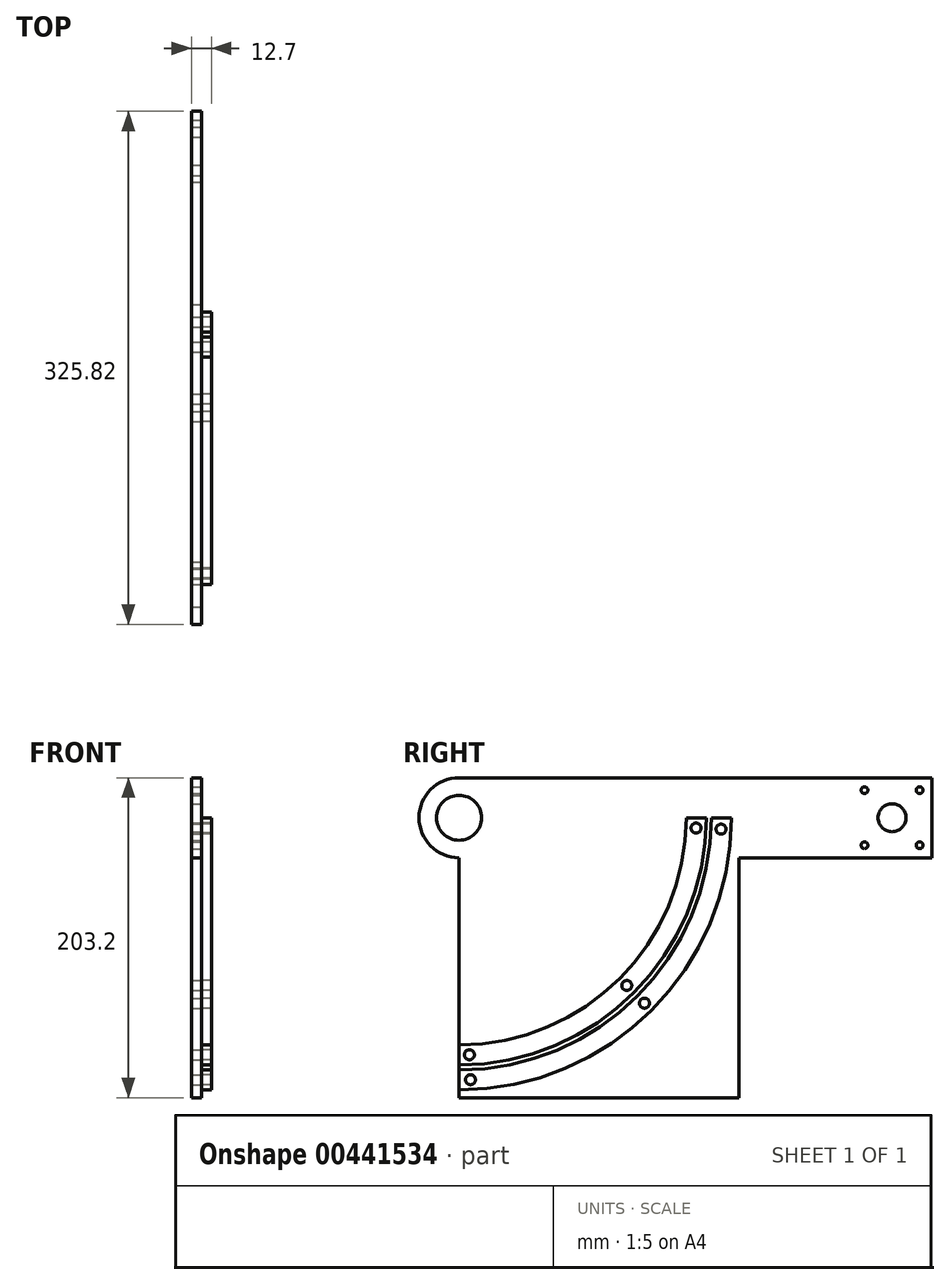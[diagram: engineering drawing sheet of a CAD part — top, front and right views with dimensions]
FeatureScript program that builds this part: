
annotation { "Feature Type Name" : "Feature", "Feature Type Description" : "" }
export const myFeature = defineFeature(function(context is Context, id is Id, definition is map)
    precondition{}
    {
        {
            var Q0;
            Q0=qCreatedBy(makeId("Right.planeOp"),FACE);
            var sketch = newSketch(context, id + "F0", { "sketchPlane" : qUnion([Q0])});
            skCircle(sketch, "E0", {"center": v(-106.55, 177.8) * mm, "radius": 25.4 * mm});
            skCircle(sketch, "E1", {"center": v(-106.55, 177.8) * mm, "radius": 14.29 * mm});
            skLineSegment(sketch, "E2.bottom", {"start": v(-106.55, 177.8) * mm, "end": v(71.25, 177.8) * mm});
            skLineSegment(sketch, "E2.top", {"start": v(-106.55, 0) * mm, "end": v(71.25, 0) * mm});
            skLineSegment(sketch, "E2.left", {"start": v(-106.55, 177.8) * mm, "end": v(-106.55, 0) * mm});
            skLineSegment(sketch, "E2.right", {"start": v(71.25, 177.8) * mm, "end": v(71.25, 0) * mm});
            skCircle(sketch, "E3", {"center": v(168.47, 177.8) * mm, "radius": 8.9 * mm});
            skLineSegment(sketch, "E4.bottom", {"start": v(185.97, 195.3) * mm, "end": v(150.97, 195.3) * mm, "construction": true});
            skLineSegment(sketch, "E4.top", {"start": v(185.97, 160.3) * mm, "end": v(150.97, 160.3) * mm, "construction": true});
            skLineSegment(sketch, "E4.left", {"start": v(185.97, 195.3) * mm, "end": v(185.97, 160.3) * mm, "construction": true});
            skLineSegment(sketch, "E4.right", {"start": v(150.97, 195.3) * mm, "end": v(150.97, 160.3) * mm, "construction": true});
            skCircle(sketch, "E5", {"center": v(185.97, 195.3) * mm, "radius": 2.16 * mm});
            skCircle(sketch, "E6", {"center": v(185.97, 160.3) * mm, "radius": 2.16 * mm});
            skCircle(sketch, "E7", {"center": v(150.97, 160.3) * mm, "radius": 2.16 * mm});
            skCircle(sketch, "E8", {"center": v(150.97, 195.3) * mm, "radius": 2.16 * mm});
            skArc(sketch, "E9", {"start": v(-106.55, 20.76) * mm, "mid": v(4.5, 66.76) * mm, "end": v(50.48, 177.8) * mm});
            skArc(sketch, "E10.0", {"start": v(-106.55, 11.24) * mm, "mid": v(11.23, 60.02) * mm, "end": v(60, 177.8) * mm, "construction": true});
            skArc(sketch, "E11.0", {"start": v(-106.55, 27.11) * mm, "mid": v(0, 71.25) * mm, "end": v(44.13, 177.8) * mm, "construction": true});
            skCircle(sketch, "E12", {"center": v(-99.98, 27.26) * mm, "radius": 3.18 * mm});
            skCircle(sketch, "E13", {"center": v(-99.29, 11.4) * mm, "radius": 3.18 * mm});
            skCircle(sketch, "E14", {"center": v(0, 71.25) * mm, "radius": 3.18 * mm});
            skCircle(sketch, "E15", {"center": v(11.23, 60.02) * mm, "radius": 3.18 * mm});
            skCircle(sketch, "E16", {"center": v(44, 171.23) * mm, "radius": 3.18 * mm});
            skCircle(sketch, "E17", {"center": v(59.85, 170.53) * mm, "radius": 3.18 * mm});
            skLineSegment(sketch, "E18", {"start": v(-106.55, 177.8) * mm, "end": v(59.85, 170.53) * mm, "construction": true});
            skLineSegment(sketch, "E19", {"start": v(11.23, 60.02) * mm, "end": v(-106.55, 177.8) * mm, "construction": true});
            skLineSegment(sketch, "E20", {"start": v(-99.29, 11.4) * mm, "end": v(-106.55, 177.8) * mm, "construction": true});
            skArc(sketch, "E21.0", {"start": v(-106.55, 33.46) * mm, "mid": v(-4.5, 75.74) * mm, "end": v(37.78, 177.8) * mm});
            skArc(sketch, "E22.0", {"start": v(-106.55, 17.59) * mm, "mid": v(6.74, 64.51) * mm, "end": v(53.66, 177.8) * mm});
            skArc(sketch, "E23.0", {"start": v(-106.55, 4.89) * mm, "mid": v(15.72, 55.53) * mm, "end": v(66.36, 177.8) * mm});
            skLineSegment(sketch, "E24", {"start": v(168.47, 177.8) * mm, "end": v(71.25, 177.8) * mm, "construction": true});
            skLineSegment(sketch, "E25.bottom", {"start": v(71.25, 152.4) * mm, "end": v(193.87, 152.4) * mm});
            skLineSegment(sketch, "E25.top", {"start": v(71.25, 203.2) * mm, "end": v(193.87, 203.2) * mm});
            skLineSegment(sketch, "E25.left", {"start": v(71.25, 152.4) * mm, "end": v(71.25, 203.2) * mm});
            skLineSegment(sketch, "E25.right", {"start": v(193.87, 152.4) * mm, "end": v(193.87, 203.2) * mm});
            skPoint(sketch, "E26", {"position": v(71.25, 177.8) * mm});
            skLineSegment(sketch, "E27", {"start": v(71.25, 203.2) * mm, "end": v(-106.55, 203.2) * mm});
            skSolve(sketch);
        }
        {
            var Q0;
            {var subQ5=sQuery(id+"F0.wireOp",EDGE,"E0");var subQ8=makeQuery(id+"F0.imprint","INTERSECT",VERTEX,{"derivedFrom":[subQ5,sQuery(id+"F0.wireOp",EDGE,"E27")]});Q0=makeQuery(id+"F0.imprint","IMPRINT",FACE,{"disambiguationData":[TD([[makeQuery(id+"F0.imprint","IMPRINT",EDGE,{"disambiguationData":[TD([[subQ8,1.0]])],"derivedFrom":subQ5}),1.0]])]});}
            var Q1;
            {var subQ0=sQuery(id+"F0.wireOp",EDGE,"E2.left");var subQ1=sQuery(id+"F0.wireOp",EDGE,"E0");var subQ2=makeQuery(id+"F0.imprint","INTERSECT",VERTEX,{"derivedFrom":[subQ1,subQ0]});Q1=makeQuery(id+"F0.imprint","IMPRINT",FACE,{"disambiguationData":[TD([[makeQuery(id+"F0.imprint","IMPRINT",EDGE,{"disambiguationData":[TD([[subQ2,-1.0]])],"derivedFrom":subQ1}),1.0]])]});}
            var Q2;
            {var subQ4=sQuery(id+"F0.wireOp",EDGE,"E27");Q2=makeQuery(id+"F0.imprint","IMPRINT",FACE,{"disambiguationData":[TD([[makeQuery(id+"F0.imprint","IMPRINT",EDGE,{"derivedFrom":subQ4}),1.0]])]});}
            var Q3;
            Q3=makeQuery(id+"F0.imprint","IMPRINT",FACE,{"disambiguationData":[TD([[makeQuery(id+"F0.imprint","IMPRINT",EDGE,{"derivedFrom":sQuery(id+"F0.wireOp",EDGE,"E3")}),-1.0]])]});
            var Q4;
            {var subQ2=sQuery(id+"F0.wireOp",EDGE,"E2.top");Q4=makeQuery(id+"F0.imprint","IMPRINT",FACE,{"disambiguationData":[TD([[makeQuery(id+"F0.imprint","IMPRINT",EDGE,{"derivedFrom":subQ2}),1.0]])]});}
            var Q5;
            Q5=makeQuery(id+"F0.imprint","IMPRINT",FACE,{"disambiguationData":[TD([[makeQuery(id+"F0.imprint","IMPRINT",EDGE,{"derivedFrom":sQuery(id+"F0.wireOp",EDGE,"E13")}),-1.0]])]});
            var Q6;
            {var subQ0=sQuery(id+"F0.wireOp",EDGE,"E9");Q6=makeQuery(id+"F0.imprint","IMPRINT",FACE,{"disambiguationData":[TD([[makeQuery(id+"F0.imprint","IMPRINT",EDGE,{"derivedFrom":subQ0}),-1.0]])]});}
            var Q7;
            {var subQ0=sQuery(id+"F0.wireOp",EDGE,"E9");Q7=makeQuery(id+"F0.imprint","IMPRINT",FACE,{"disambiguationData":[TD([[makeQuery(id+"F0.imprint","IMPRINT",EDGE,{"derivedFrom":subQ0}),1.0]])]});}
            var Q8;
            {var subQ5=sQuery(id+"F0.wireOp",EDGE,"E21.0");Q8=makeQuery(id+"F0.imprint","IMPRINT",FACE,{"disambiguationData":[TD([[makeQuery(id+"F0.imprint","IMPRINT",EDGE,{"derivedFrom":subQ5}),1.0]])]});}
            extrude(context, id + "F1", {"entities" : qUnion([Q0, Q1, Q2, Q3, Q4, Q5, Q6, Q7, Q8]), "oppositeDirection" : true, "depth" : 6.35 * mm, "offsetDistance" : 25.4 * mm});
        }
        {
            var Q0;
            {var subQ0=sQuery(id+"F0.wireOp",EDGE,"E9");Q0=makeQuery(id+"F0.imprint","IMPRINT",FACE,{"disambiguationData":[TD([[makeQuery(id+"F0.imprint","IMPRINT",EDGE,{"derivedFrom":subQ0}),1.0]])]});}
            extrude(context, id + "F2", {"entities" : qUnion([Q0]), "depth" : 6.35 * mm, "offsetDistance" : 25.4 * mm});
        }
        {
            var Q0;
            Q0=makeQuery(id+"F0.imprint","IMPRINT",FACE,{"disambiguationData":[TD([[makeQuery(id+"F0.imprint","IMPRINT",EDGE,{"derivedFrom":sQuery(id+"F0.wireOp",EDGE,"E13")}),-1.0]])]});
            extrude(context, id + "F3", {"entities" : qUnion([Q0]), "depth" : 6.35 * mm, "offsetDistance" : 25.4 * mm});
        }
    });
